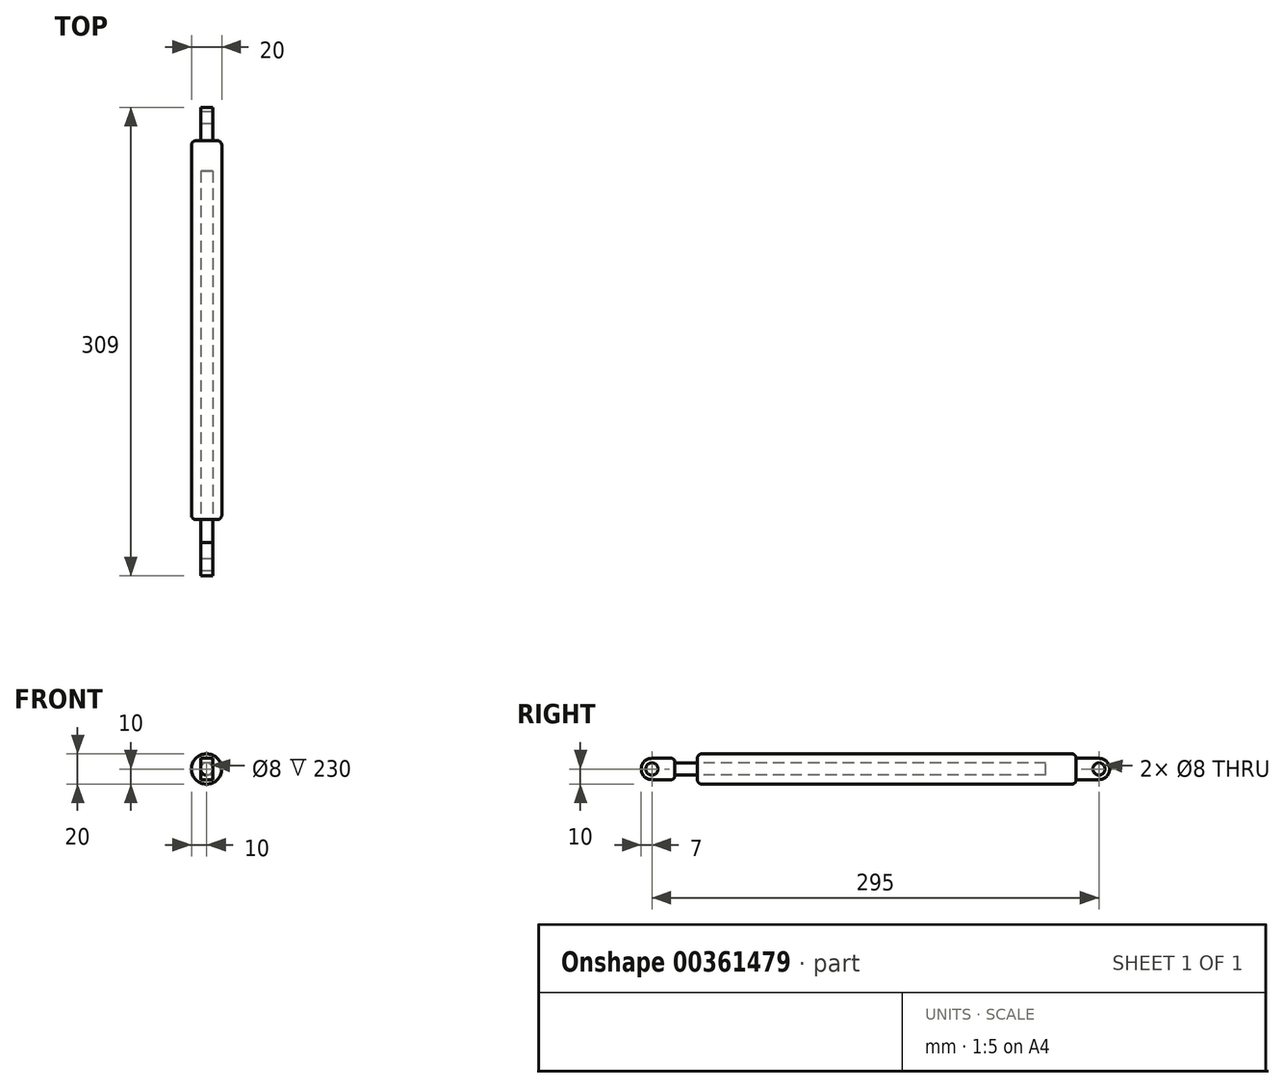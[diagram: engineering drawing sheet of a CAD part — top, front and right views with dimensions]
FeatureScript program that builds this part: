
annotation { "Feature Type Name" : "Feature", "Feature Type Description" : "" }
export const myFeature = defineFeature(function(context is Context, id is Id, definition is map)
    precondition{}
    {
        {
            var Q0;
            Q0=qCreatedBy(makeId("Front.planeOp"),FACE);
            var sketch = newSketch(context, id + "F0", { "sketchPlane" : qUnion([Q0])});
            skCircle(sketch, "E0", {"center": v(0, 0) * mm, "radius": 4 * mm});
            skCircle(sketch, "E1", {"center": v(0, 0) * mm, "radius": 10 * mm});
            skSolve(sketch);
        }
        {
            var Q0;
            Q0=makeQuery(id+"F0.imprint","IMPRINT",FACE,{"disambiguationData":[TD([[makeQuery(id+"F0.imprint","IMPRINT",EDGE,{"derivedFrom":sQuery(id+"F0.wireOp",EDGE,"E0")}),-1.0]])]});
            var Q1;
            Q1=makeQuery(id+"F0.imprint","IMPRINT",FACE,{"disambiguationData":[TD([[makeQuery(id+"F0.imprint","IMPRINT",EDGE,{"derivedFrom":sQuery(id+"F0.wireOp",EDGE,"E0")}),1.0]])]});
            extrude(context, id + "F1", {"entities" : qUnion([Q0, Q1]), "oppositeDirection" : true, "depth" : 250 * mm});
        }
        {
            var Q0;
            Q0=makeQuery(id+"F0.imprint","IMPRINT",FACE,{"disambiguationData":[TD([[makeQuery(id+"F0.imprint","IMPRINT",EDGE,{"derivedFrom":sQuery(id+"F0.wireOp",EDGE,"E0")}),1.0]])]});
            extrude(context, id + "F2", {"entities" : qUnion([Q0]), "operationType" : NewBodyOperationType.REMOVE, "oppositeDirection" : true, "depth" : 230 * mm});
        }
        {
            var Q0;
            Q0=makeQuery(id+"F0.imprint","IMPRINT",FACE,{"disambiguationData":[TD([[makeQuery(id+"F0.imprint","IMPRINT",EDGE,{"derivedFrom":sQuery(id+"F0.wireOp",EDGE,"E0")}),1.0]])]});
            extrude(context, id + "F3", {"entities" : qUnion([Q0]), "oppositeDirection" : true, "depth" : 230 * mm, "hasSecondDirection" : true, "secondDirectionOppositeDirection" : false, "secondDirectionDepth" : 15 * mm});
        }
        {
            var Q0;
            Q0=makeQuery(id+"F1.opExtrude","CAP_EDGE",EDGE,{"disambiguationData":[OSD([sQuery(id+"F0.wireOp",EDGE,"E1")])],"isStart":true});
            var Q1;
            Q1=makeQuery(id+"F1.opExtrude","CAP_EDGE",EDGE,{"disambiguationData":[OSD([sQuery(id+"F0.wireOp",EDGE,"E1")])],"isStart":false});
            fillet(context, id + "F4", {"entities" : qUnion([Q0, Q1]), "radius" : 3 * mm, "tangentPropagation" : true, "allowEdgeOverflow" : false});
        }
        {
            var Q0;
            Q0=qCreatedBy(makeId("Right.planeOp"),FACE);
            var sketch = newSketch(context, id + "F5", { "sketchPlane" : qUnion([Q0])});
            skLineSegment(sketch, "E2.0", {"start": v(250, 7) * mm, "end": v(250, -7) * mm});
            skLineSegment(sketch, "E3.bottom", {"start": v(250, 7) * mm, "end": v(265, 7) * mm});
            skLineSegment(sketch, "E3.top", {"start": v(250, -7) * mm, "end": v(265, -7) * mm});
            skLineSegment(sketch, "E3.right", {"start": v(272, 0) * mm, "end": v(272, 0) * mm});
            skPoint(sketch, "E4.visualSharp", {"position": v(272, 7) * mm});
            skArc(sketch, "E4.filletArc", {"start": v(272, 0) * mm, "mid": v(269.95, 4.95) * mm, "end": v(265, 7) * mm});
            skPoint(sketch, "E5.visualSharp", {"position": v(272, -7) * mm});
            skArc(sketch, "E5.filletArc", {"start": v(265, -7) * mm, "mid": v(269.95, -4.95) * mm, "end": v(272, 0) * mm});
            skCircle(sketch, "E6", {"center": v(265, 0) * mm, "radius": 4 * mm});
            skSolve(sketch);
        }
        {
            var Q0;
            Q0 = qSketchRegion(id + "F5", true);
            extrude(context, id + "F6", {"entities" : qUnion([Q0]), "operationType" : NewBodyOperationType.ADD, "endBound" : BoundingType.SYMMETRIC, "depth" : 8 * mm});
        }
        {
            var Q0;
            Q0=qCreatedBy(makeId("Right.planeOp"),FACE);
            var sketch = newSketch(context, id + "F7", { "sketchPlane" : qUnion([Q0])});
            skLineSegment(sketch, "E7.0", {"start": v(-15, -4) * mm, "end": v(-15, 4) * mm});
            skLineSegment(sketch, "E8.bottom", {"start": v(-15, -7) * mm, "end": v(-30, -7) * mm});
            skLineSegment(sketch, "E8.top", {"start": v(-15, 7) * mm, "end": v(-30, 7) * mm});
            skLineSegment(sketch, "E8.left", {"start": v(-15, -7) * mm, "end": v(-15, 7) * mm});
            skLineSegment(sketch, "E8.right", {"start": v(-37, 0) * mm, "end": v(-37, 0) * mm});
            skCircle(sketch, "E9", {"center": v(-30, 0) * mm, "radius": 4 * mm});
            skPoint(sketch, "E9.centerSnap0", {"position": v(-37, 0) * mm});
            skPoint(sketch, "E10.visualSharp", {"position": v(-37, 7) * mm});
            skArc(sketch, "E10.filletArc", {"start": v(-30, 7) * mm, "mid": v(-34.95, 4.95) * mm, "end": v(-37, 0) * mm});
            skPoint(sketch, "E11.visualSharp", {"position": v(-37, -7) * mm});
            skArc(sketch, "E11.filletArc", {"start": v(-37, 0) * mm, "mid": v(-34.95, -4.95) * mm, "end": v(-30, -7) * mm});
            skSolve(sketch);
        }
        {
            var Q0;
            {var subQ1=sQuery(id+"F7.wireOp",EDGE,"E8.bottom");Q0=makeQuery(id+"F7.imprint","IMPRINT",FACE,{"disambiguationData":[TD([[makeQuery(id+"F7.imprint","IMPRINT",EDGE,{"derivedFrom":subQ1}),-1.0]])]});}
            extrude(context, id + "F8", {"entities" : qUnion([Q0]), "operationType" : NewBodyOperationType.ADD, "endBound" : BoundingType.SYMMETRIC, "depth" : 8 * mm});
        }
        {
            var Q0;
            Q0=makeQuery(id+"F8.opExtrude","SWEPT_EDGE",EDGE,{"disambiguationData":[OSD([sQuery(id+"F7.wireOp",EDGE,"E8.top"),sQuery(id+"F7.wireOp",EDGE,"E8.left")])]});
            var Q1;
            Q1=makeQuery(id+"F8.opExtrude","SWEPT_EDGE",EDGE,{"disambiguationData":[OSD([sQuery(id+"F7.wireOp",EDGE,"E8.bottom"),sQuery(id+"F7.wireOp",EDGE,"E8.left")])]});
            fillet(context, id + "F9", {"entities" : qUnion([Q0, Q1]), "radius" : 2 * mm, "tangentPropagation" : true, "allowEdgeOverflow" : false});
        }
        {
            var Q0;
            Q0=makeQuery(id+"F1.opExtrude","SWEPT_BODY",BODY,{"disambiguationData":[OSD([sQuery(id+"F0.wireOp",EDGE,"E1")])]});
            transform(context, id + "F10", {"entities" : qUnion([Q0]), "transformType" : TransformType.TRANSLATION_3D, "dx" : 200 * mm, "dy" : 0 * mm, "dz" : 0 * mm, "makeCopy" : true});
        }
        {
            var Q0;
            Q0=makeQuery(id+"F3.opExtrude","SWEPT_BODY",BODY,{"disambiguationData":[OSD([sQuery(id+"F0.wireOp",EDGE,"E0")])]});
            transform(context, id + "F11", {"entities" : qUnion([Q0]), "transformType" : TransformType.TRANSLATION_3D, "dx" : 200 * mm, "dy" : 0 * mm, "dz" : 0 * mm, "makeCopy" : true});
        }
        {
            var Q0;
            Q0=makeQuery(id+"F11.opPattern","COPY",BODY,{"derivedFrom":makeQuery(id+"F3.opExtrude","SWEPT_BODY",BODY,{"disambiguationData":[OSD([sQuery(id+"F0.wireOp",EDGE,"E0")])]}),"instanceName":"1"});
            deleteBodies(context, id + "F12", {"entities" : qUnion([Q0])});
        }
        {
            var Q0;
            Q0=makeQuery(id+"F10.opPattern","COPY",BODY,{"derivedFrom":makeQuery(id+"F1.opExtrude","SWEPT_BODY",BODY,{"disambiguationData":[OSD([sQuery(id+"F0.wireOp",EDGE,"E1")])]}),"instanceName":"1"});
            deleteBodies(context, id + "F13", {"entities" : qUnion([Q0])});
        }
    });
